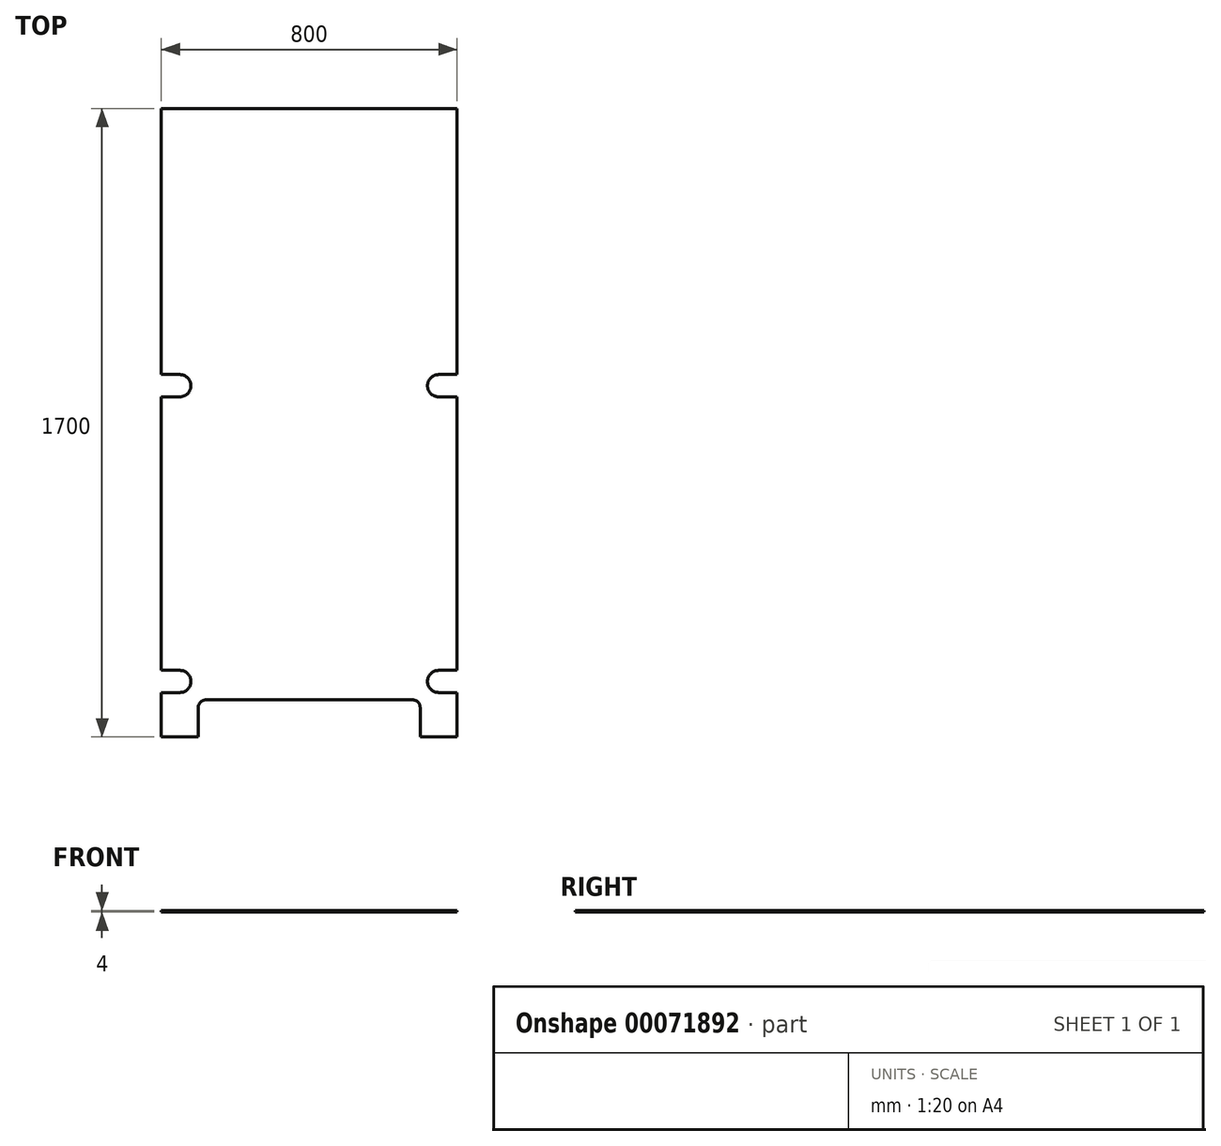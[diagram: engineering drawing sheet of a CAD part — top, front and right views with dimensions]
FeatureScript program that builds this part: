
annotation { "Feature Type Name" : "Feature", "Feature Type Description" : "" }
export const myFeature = defineFeature(function(context is Context, id is Id, definition is map)
    precondition{}
    {
        {
            var Q0;
            Q0=qCreatedBy(makeId("Top.planeOp"),FACE);
            var sketch = newSketch(context, id + "F0", { "sketchPlane" : qUnion([Q0])});
            skLineSegment(sketch, "E0.bottom", {"start": v(400, -850) * mm, "end": v(300, -850) * mm});
            skLineSegment(sketch, "E0.top", {"start": v(400, 850) * mm, "end": v(-400, 850) * mm});
            skLineSegment(sketch, "E0.left", {"start": v(400, -850) * mm, "end": v(400, -730) * mm});
            skLineSegment(sketch, "E0.right", {"start": v(-400, -850) * mm, "end": v(-400, -730) * mm});
            skPoint(sketch, "E0.middle", {"position": v(0, 0) * mm});
            skLineSegment(sketch, "E1", {"start": v(-537.18, -700) * mm, "end": v(560.34, -700) * mm, "construction": true});
            skLineSegment(sketch, "E2", {"start": v(-379.85, 100) * mm, "end": v(668.08, 100) * mm, "construction": true});
            skLineSegment(sketch, "E3", {"start": v(-494.06, 450) * mm, "end": v(586.21, 450) * mm, "construction": true});
            skLineSegment(sketch, "E4", {"start": v(-350, -670) * mm, "end": v(-400, -670) * mm});
            skLineSegment(sketch, "E5.MirrorCS", {"start": v(-350, -730) * mm, "end": v(-400, -730) * mm});
            skArc(sketch, "E6", {"start": v(-350, -730) * mm, "mid": v(-320, -700) * mm, "end": v(-350, -670) * mm});
            skPoint(sketch, "E7.orphan", {"position": v(-573, -670) * mm});
            skPoint(sketch, "E8.orphan", {"position": v(-573, -730) * mm});
            skLineSegment(sketch, "E9.trimOffspring", {"start": v(-400, -670) * mm, "end": v(-400, 70.08) * mm});
            skLineSegment(sketch, "E10.MirrorCS", {"start": v(350, -730) * mm, "end": v(400, -730) * mm});
            skLineSegment(sketch, "E11.MirrorCS", {"start": v(350, -670) * mm, "end": v(400, -670) * mm});
            skArc(sketch, "E12.MirrorCS", {"start": v(350, -730) * mm, "mid": v(320, -700) * mm, "end": v(350, -670) * mm});
            skLineSegment(sketch, "E13.trimOffspring", {"start": v(400, -670) * mm, "end": v(400, 70.08) * mm});
            skArc(sketch, "E14", {"start": v(-352.18, 70.08) * mm, "mid": v(-320.03, 98.68) * mm, "end": v(-349.55, 130) * mm});
            skLineSegment(sketch, "E15", {"start": v(-349.55, 130) * mm, "end": v(-400, 130.75) * mm});
            skLineSegment(sketch, "E16", {"start": v(-352.18, 70.08) * mm, "end": v(-400, 70.08) * mm});
            skLineSegment(sketch, "E17.trimOffspring", {"start": v(-400, 130.75) * mm, "end": v(-400, 850) * mm});
            skLineSegment(sketch, "E18.MirrorCS", {"start": v(349.55, 130) * mm, "end": v(400, 130.75) * mm});
            skLineSegment(sketch, "E19.MirrorCS", {"start": v(352.18, 70.08) * mm, "end": v(400, 70.08) * mm});
            skArc(sketch, "E20.MirrorCS", {"start": v(352.18, 70.08) * mm, "mid": v(320.03, 98.68) * mm, "end": v(349.55, 130) * mm});
            skLineSegment(sketch, "E21.trimOffspring", {"start": v(400, 130.75) * mm, "end": v(400, 850) * mm});
            skLineSegment(sketch, "E22", {"start": v(0, -736.55) * mm, "end": v(0, -373.87) * mm, "construction": true});
            skPoint(sketch, "E22.startSnap0", {"position": v(0, -850) * mm});
            skLineSegment(sketch, "E23", {"start": v(-300, -850) * mm, "end": v(-300, -770) * mm});
            skLineSegment(sketch, "E24", {"start": v(-280, -750) * mm, "end": v(280, -750) * mm});
            skLineSegment(sketch, "E25", {"start": v(300, -770) * mm, "end": v(300, -850) * mm});
            skLineSegment(sketch, "E26.trimOffspring", {"start": v(-300, -850) * mm, "end": v(-400, -850) * mm});
            skPoint(sketch, "E27.visualSharp", {"position": v(-300, -750) * mm});
            skArc(sketch, "E27.filletArc", {"start": v(-280, -750) * mm, "mid": v(-294.14, -755.86) * mm, "end": v(-300, -770) * mm});
            skPoint(sketch, "E28.visualSharp", {"position": v(300, -750) * mm});
            skArc(sketch, "E28.filletArc", {"start": v(300, -770) * mm, "mid": v(294.14, -755.86) * mm, "end": v(280, -750) * mm});
            skSolve(sketch);
        }
        {
            var Q0;
            Q0 = qSketchRegion(id + "F0", true);
            extrude(context, id + "F1", {"entities" : qUnion([Q0]), "depth" : 4 * mm});
        }
    });
